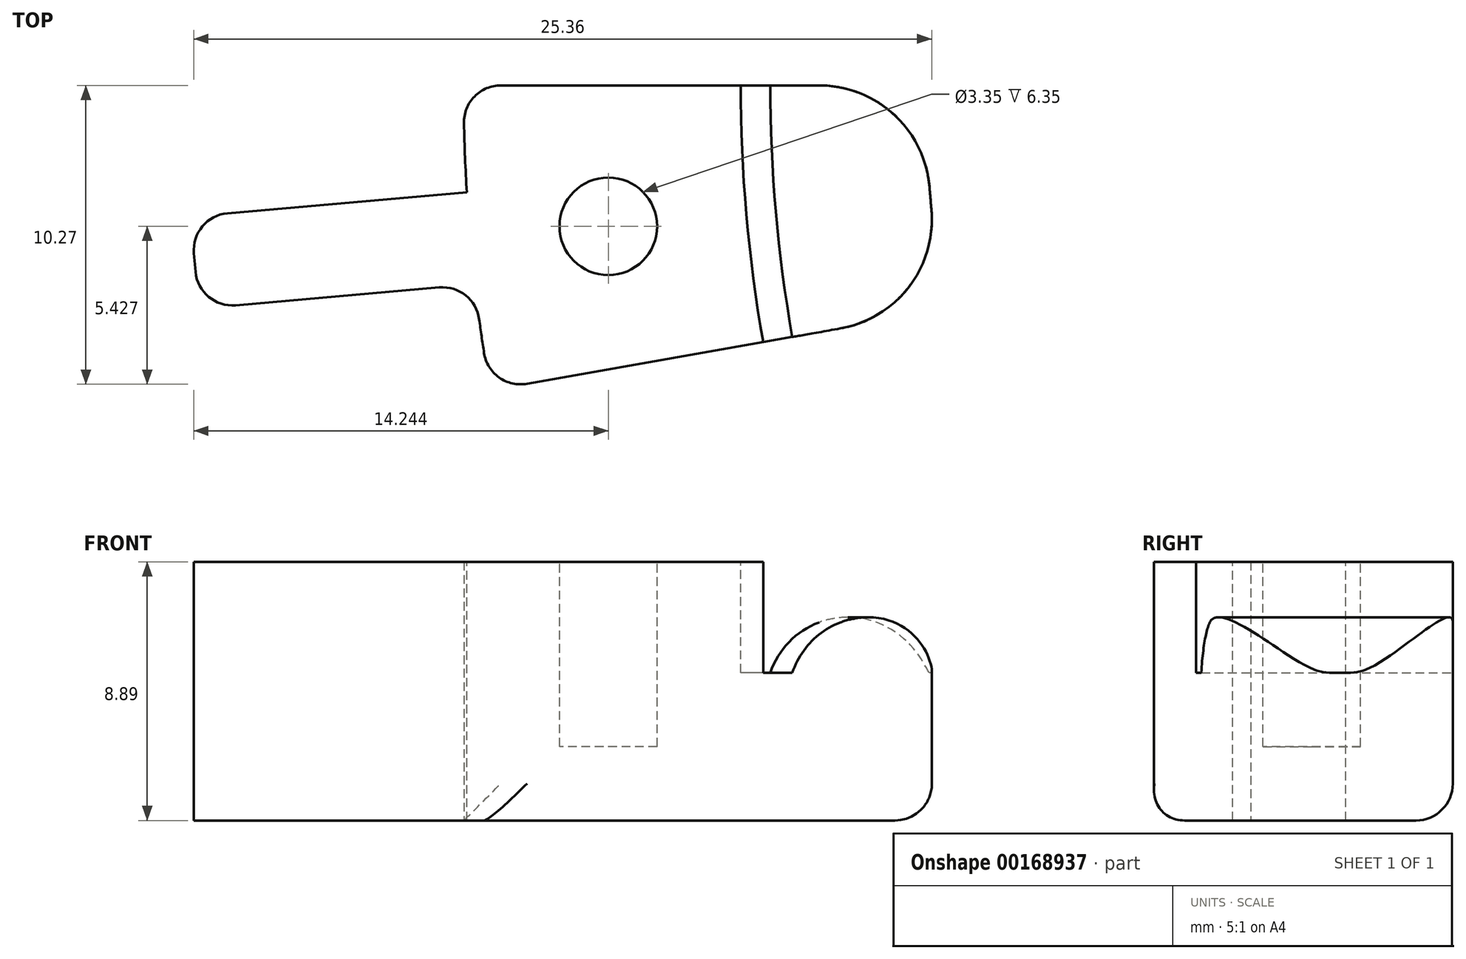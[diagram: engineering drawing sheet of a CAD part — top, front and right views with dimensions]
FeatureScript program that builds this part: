
annotation { "Feature Type Name" : "Feature", "Feature Type Description" : "" }
export const myFeature = defineFeature(function(context is Context, id is Id, definition is map)
    precondition{}
    {
        {
            var Q0;
            Q0=qCreatedBy(makeId("Front.planeOp"),FACE);
            var sketch = newSketch(context, id + "F0", { "sketchPlane" : qUnion([Q0])});
            skLineSegment(sketch, "E0", {"start": v(10.54, 5.08) * mm, "end": v(9.53, 5.08) * mm});
            skLineSegment(sketch, "E1", {"start": v(9.53, 5.08) * mm, "end": v(9.53, 8.9) * mm});
            skLineSegment(sketch, "E2", {"start": v(9.53, 8.9) * mm, "end": v(0, 8.9) * mm});
            skLineSegment(sketch, "E3", {"start": v(0, 8.9) * mm, "end": v(0, 0) * mm});
            skLineSegment(sketch, "E4", {"start": v(0, 0) * mm, "end": v(15.88, 0) * mm});
            skLineSegment(sketch, "E5", {"start": v(15.88, 0) * mm, "end": v(15.88, 5.08) * mm});
            skArc(sketch, "E6", {"start": v(15.88, 5.08) * mm, "mid": v(13.2, 6.99) * mm, "end": v(10.54, 5.08) * mm});
            skLineSegment(sketch, "E7", {"start": v(13.2, 6.99) * mm, "end": v(0, 6.99) * mm, "construction": true});
            skSolve(sketch);
        }
        {
            var Q0;
            Q0=qCreatedBy(makeId("Top.planeOp"),FACE);
            var sketch = newSketch(context, id + "F1", { "sketchPlane" : qUnion([Q0])});
            skCircle(sketch, "E8", {"center": v(60.33, 0) * mm, "radius": 50.8 * mm});
            skSolve(sketch);
        }
        {
            var Q0;
            Q0=makeQuery(id+"F0.imprint","IMPRINT",FACE,{"disambiguationData":[TD([[makeQuery(id+"F0.imprint","IMPRINT",EDGE,{"derivedFrom":sQuery(id+"F0.wireOp",EDGE,"E0")}),1.0]])]});
            var Q1;
            Q1=sQuery(id+"F1.wireOp",EDGE,"E8");
            revolve(context, id + "F2", {"entities" : qUnion([Q0]), "axis" : qUnion([Q1]), "revolveType" : RevolveType.ONE_DIRECTION, "angle" : 10 * degree});
        }
        {
            var Q0;
            Q0=makeQuery(id+"F2.opRevolve","SWEPT_FACE",FACE,{"disambiguationData":[OSD([sQuery(id+"F0.wireOp",EDGE,"E2")])]});
            var sketch = newSketch(context, id + "F3", { "sketchPlane" : qUnion([Q0])});
            skCircle(sketch, "E9", {"center": v(4.97, -4.84) * mm, "radius": 1.68 * mm});
            skCircle(sketch, "E10", {"center": v(60.33, 0) * mm, "radius": 55.56 * mm, "construction": true});
            skLineSegment(sketch, "E11", {"start": v(9.72, -4.43) * mm, "end": v(0.23, -5.26) * mm, "construction": true});
            skSolve(sketch);
        }
        {
            var Q0;
            Q0=makeQuery(id+"F3.imprint","IMPRINT",FACE,{"disambiguationData":[TD([[makeQuery(id+"F3.imprint","IMPRINT",EDGE,{"derivedFrom":sQuery(id+"F3.wireOp",EDGE,"E9")}),1.0]])]});
            extrude(context, id + "F4", {"entities" : qUnion([Q0]), "operationType" : NewBodyOperationType.REMOVE, "oppositeDirection" : true, "depth" : 6.35 * mm});
        }
        {
            var Q0;
            Q0=makeQuery(id+"F2.opRevolve","CAP_EDGE",EDGE,{"disambiguationData":[OSD([sQuery(id+"F0.wireOp",EDGE,"E3")])],"isStart":false});
            var Q1;
            Q1=makeQuery(id+"F2.opRevolve","CAP_EDGE",EDGE,{"disambiguationData":[OSD([sQuery(id+"F0.wireOp",EDGE,"E3")])],"isStart":true});
            var Q2;
            Q2=makeQuery(id+"F2.opRevolve","CAP_EDGE",EDGE,{"disambiguationData":[OSD([sQuery(id+"F0.wireOp",EDGE,"E4")])],"isStart":false});
            var Q3;
            Q3=makeQuery(id+"F2.opRevolve","CAP_EDGE",EDGE,{"disambiguationData":[OSD([sQuery(id+"F0.wireOp",EDGE,"E4")])],"isStart":true});
            var Q4;
            Q4=makeQuery(id+"F2.opRevolve","SWEPT_EDGE",EDGE,{"disambiguationData":[OSD([sQuery(id+"F0.wireOp",EDGE,"E4"),sQuery(id+"F0.wireOp",EDGE,"E5")])]});
            fillet(context, id + "F5", {"entities" : qUnion([Q0, Q1, Q2, Q3, Q4]), "radius" : 1.27 * mm, "tangentPropagation" : true, "allowEdgeOverflow" : false});
        }
        {
            var Q0;
            Q0=makeQuery(id+"F2.opRevolve","SWEPT_FACE",FACE,{"disambiguationData":[OSD([sQuery(id+"F0.wireOp",EDGE,"E2")])]});
            var sketch = newSketch(context, id + "F6", { "sketchPlane" : qUnion([Q0])});
            skLineSegment(sketch, "E12", {"start": v(0.11, -3.67) * mm, "end": v(-9.38, -4.5) * mm});
            skLineSegment(sketch, "E13", {"start": v(-9.38, -4.5) * mm, "end": v(-9.1, -7.67) * mm});
            skLineSegment(sketch, "E14", {"start": v(-9.1, -7.67) * mm, "end": v(0.39, -6.84) * mm});
            skLineSegment(sketch, "E15", {"start": v(4.97, -4.84) * mm, "end": v(0.23, -5.26) * mm, "construction": true});
            skSolve(sketch);
        }
        {
            var Q0;
            {var subQ0=sQuery(id+"F6.wireOp",EDGE,"E12");Q0=makeQuery(id+"F6.imprint","IMPRINT",FACE,{"disambiguationData":[TD([[makeQuery(id+"F6.imprint","IMPRINT",EDGE,{"derivedFrom":subQ0}),1.0]])]});}
            var Q1;
            Q1=makeQuery(id+"F2.opRevolve","SWEPT_FACE",FACE,{"disambiguationData":[OSD([sQuery(id+"F0.wireOp",EDGE,"E4")])]});
            extrude(context, id + "F7", {"entities" : qUnion([Q0]), "operationType" : NewBodyOperationType.ADD, "endBound" : BoundingType.UP_TO_SURFACE, "oppositeDirection" : true, "endBoundEntityFace" : qUnion([Q1]), "depth" : 25.4 * mm});
        }
        {
            var Q0;
            Q0=makeQuery(id+"F7.opExtrude","SWEPT_EDGE",EDGE,{"disambiguationData":[OSD([sQuery(id+"F0.wireOp",EDGE,"E2"),sQuery(id+"F0.wireOp",EDGE,"E3"),sQuery(id+"F6.wireOp",EDGE,"E12")])]});
            var Q1;
            Q1=makeQuery(id+"F7.opExtrude","SWEPT_EDGE",EDGE,{"disambiguationData":[OSD([sQuery(id+"F0.wireOp",EDGE,"E2"),sQuery(id+"F0.wireOp",EDGE,"E3"),sQuery(id+"F6.wireOp",EDGE,"E14")])]});
            var Q2;
            Q2=makeQuery(id+"F7.opExtrude","SWEPT_EDGE",EDGE,{"disambiguationData":[OSD([sQuery(id+"F6.wireOp",EDGE,"E13"),sQuery(id+"F6.wireOp",EDGE,"E14")])]});
            var Q3;
            Q3=makeQuery(id+"F7.opExtrude","SWEPT_EDGE",EDGE,{"disambiguationData":[OSD([sQuery(id+"F6.wireOp",EDGE,"E12"),sQuery(id+"F6.wireOp",EDGE,"E13")])]});
            fillet(context, id + "F8", {"entities" : qUnion([Q0, Q1, Q2, Q3]), "radius" : 1.27 * mm, "tangentPropagation" : true, "allowEdgeOverflow" : false});
        }
        {
            var Q0;
            Q0=makeQuery(id+"F2.opRevolve","CAP_EDGE",EDGE,{"disambiguationData":[OSD([sQuery(id+"F0.wireOp",EDGE,"E5")])],"isStart":true});
            var Q1;
            Q1=makeQuery(id+"F2.opRevolve","CAP_EDGE",EDGE,{"disambiguationData":[OSD([sQuery(id+"F0.wireOp",EDGE,"E5")])],"isStart":false});
            fillet(context, id + "F9", {"entities" : qUnion([Q0, Q1]), "radius" : 3.8 * mm, "tangentPropagation" : true, "allowEdgeOverflow" : false});
        }
    });
